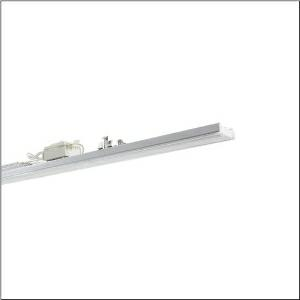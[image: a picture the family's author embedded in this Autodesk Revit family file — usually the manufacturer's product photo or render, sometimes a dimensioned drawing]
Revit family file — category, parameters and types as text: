
# Revit family: licross_11_recessed_mo_51tl1edv4e5g
name_source: partatom
category: Lighting Fixtures
units: mm (PartAtom-declared; Revit-internal decimal feet)

## family parameters
Cut with Voids When Loaded = No
Host = Face
Light Source = No
Part Type = Normal
Room Calculation Point = No
Round Connector Dimension = Use Diameter
Shared = No

## types (1)
- --- (1 x LED, 14850 lm, 84.1 W, 4000K)
    Apparent Load = 84 VA
    CIE Flux Codes = 85 95 99 100 100
    Color Rendering = 80
    Color Temperature = 4000K
    Default Elevation = 1800 mm
    Description = Licross 11 Recessed MO, luminaire insert, of sheet steel, coil coated, white, length: 2.250mm, width: 66mm, height: 67mm, LED rated luminous flux: 14.850lm, light colour: 840, SDCM (Standard Deviation of Colour Matching)MacAdam ≤ 2 SDCM (initial), control gear: DALI 2, with plug, 5-pole, with phase selection, mains connection: 220..240V, AC, 50/60Hz, rated input power: 84W, internal wiring halogen-free, primary light control with lens, of plastic, primary optical cover: cover, of PMMA, light emission: direct distribution, primary light characteristic: symmetric, protection rating (complete): IP40, insulation class (complete): insulation class I (protective earthing), certification: CE, ENEC, VDE, UKCA, protection symbol: D if used in an environment without relevant dust loads with corresponding accessories, impact resistance: IK06, permissible ambient temperature for indoor applications: -25..+35°C, corresponds to IFS (International Featured Standards) requirements for safety and quality in the food industry, reducing of maximum allowable ambient temperature of 5°C with ceiling mounting, LABS conformity tested according to VDMA 24364:2018-05, The light source and the operating device comply with the requirements of the Ecodesign Regulation (EU) 2019/2020 and are replaceable in accordance with this regulation, packaging unit: 1 piece
    Height = 58 mm
    Lamp = 1 x LED
    Lamp Light Flux = 14850 lm
    Lamp Power = 84.1 W
    Lamp count = 1
    Length = 2250 mm
    Luminous efficacy = 177 lm/W
    Manufacturer = Siteco
    ModVariant = No
    Model = 51TL1EDV4E5G
    Mounting Place = Ceiling
    Mounting Type = Pendant
    Number of Poles = 1
    OnlyDefault = Yes
    Power Factor = 1
    Product Name = Licross 11 Recessed MO
    Product group = luminaire insert | ceiling pendant
    ProductGroupID = 901
    Protection Class = Protection class I
    Protection Degree = IP 40
    RLX_Detail_Level = 1
    RLX_Emergency_Light_Flux = 0 lm
    RLX_Emergency_Type = 0
    RLX_Emergency_Type_DB = No
    RlxData = <blob elided: 30045 chars, md5=881e52fc>
    Socket = socket
    Standby Power = 0 W
    System Light Flux = 14850 lm
    System Power = 84 W
    Type Comments = factory setting: luminous flux: 100 % | dim-lin: 254 | 378 mA
    Type Image = l_1296930.jpg
    URL = http://relux.com
    VarID = @adj_099729
    Voltage = 0 V
    Weight = 0.00 kg
    Width = 66 mm

## geometry (parser evidence)
native form markers: Blend x4, Sweep x8
no freeform markers — native parametric forms only
